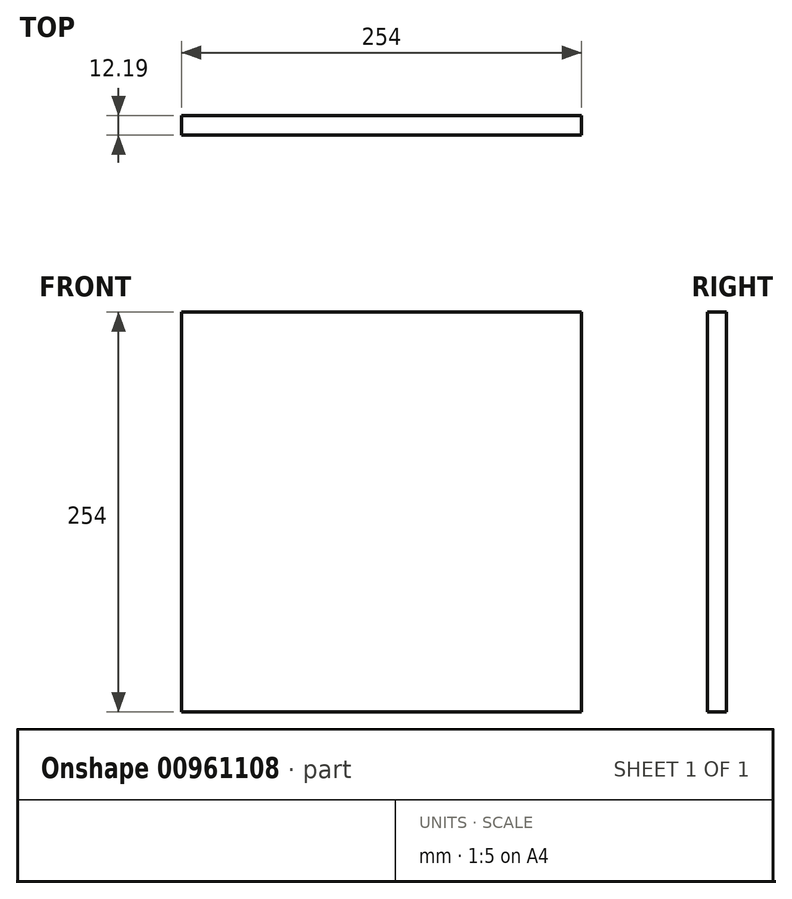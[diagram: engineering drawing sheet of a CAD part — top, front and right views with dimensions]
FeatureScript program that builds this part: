
annotation { "Feature Type Name" : "Feature", "Feature Type Description" : "" }
export const myFeature = defineFeature(function(context is Context, id is Id, definition is map)
    precondition{}
    {
        {
            var Q0;
            Q0=qCreatedBy(makeId("Front.planeOp"),FACE);
            var sketch = newSketch(context, id + "F0", { "sketchPlane" : qUnion([Q0])});
            skLineSegment(sketch, "E0.bottom", {"start": v(-127, 127) * mm, "end": v(127, 127) * mm});
            skLineSegment(sketch, "E0.top", {"start": v(-127, -127) * mm, "end": v(127, -127) * mm});
            skLineSegment(sketch, "E0.left", {"start": v(-127, 127) * mm, "end": v(-127, -127) * mm});
            skLineSegment(sketch, "E0.right", {"start": v(127, 127) * mm, "end": v(127, -127) * mm});
            skPoint(sketch, "E0.middle", {"position": v(0, 0) * mm});
            skSolve(sketch);
        }
        {
            var Q0;
            Q0=makeQuery(id+"F0.imprint","IMPRINT",FACE,{"disambiguationData":[TD([[makeQuery(id+"F0.imprint","IMPRINT",EDGE,{"derivedFrom":sQuery(id+"F0.wireOp",EDGE,"E0.bottom")}),-1.0]])]});
            extrude(context, id + "F1", {"entities" : qUnion([Q0]), "depth" : 12.2 * mm, "offsetDistance" : 25.4 * mm});
        }
    });
